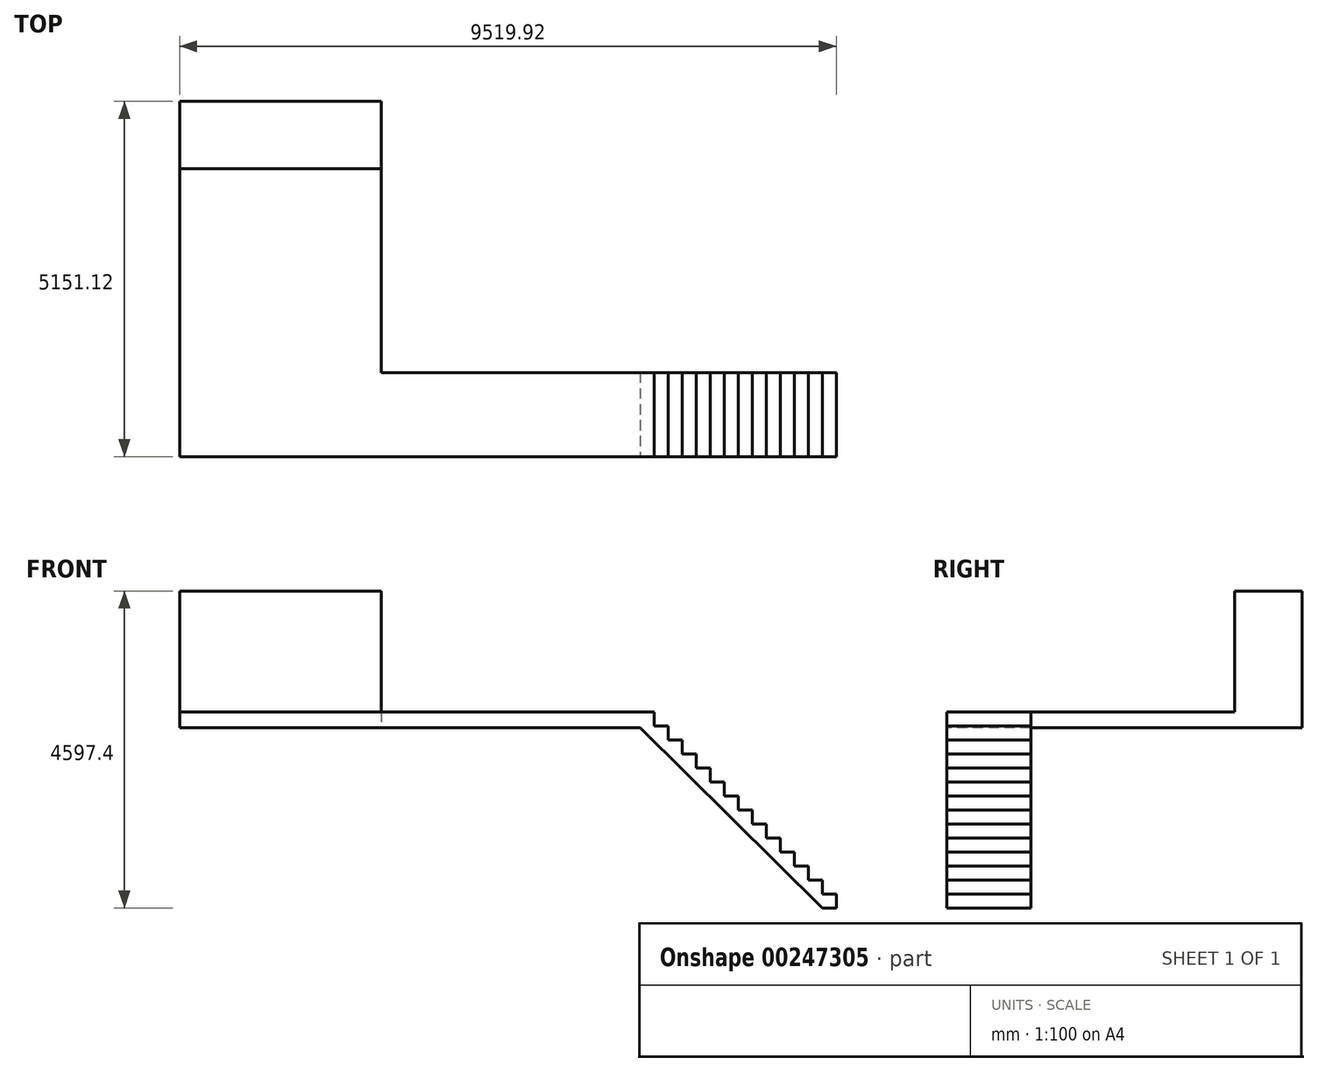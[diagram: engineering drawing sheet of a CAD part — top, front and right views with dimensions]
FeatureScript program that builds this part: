
annotation { "Feature Type Name" : "Feature", "Feature Type Description" : "" }
export const myFeature = defineFeature(function(context is Context, id is Id, definition is map)
    precondition{}
    {
        {
            var Q0;
            Q0=qCreatedBy(makeId("Top.planeOp"),FACE);
            var sketch = newSketch(context, id + "F0", { "sketchPlane" : qUnion([Q0])});
            skLineSegment(sketch, "E0.bottom", {"start": v(1463.04, -2575.56) * mm, "end": v(-1463.04, -2575.56) * mm});
            skLineSegment(sketch, "E0.top", {"start": v(1463.04, 2575.56) * mm, "end": v(-1463.04, 2575.56) * mm});
            skLineSegment(sketch, "E0.left", {"start": v(1463.04, -1356.36) * mm, "end": v(1463.04, 2575.56) * mm});
            skLineSegment(sketch, "E0.right", {"start": v(-1463.04, -2575.56) * mm, "end": v(-1463.04, 2575.56) * mm});
            skPoint(sketch, "E0.middle", {"position": v(0, 0) * mm});
            skLineSegment(sketch, "E1", {"start": v(1463.04, -1356.36) * mm, "end": v(5212.08, -1356.36) * mm});
            skLineSegment(sketch, "E2", {"start": v(1463.04, -2575.56) * mm, "end": v(5212.08, -2575.56) * mm});
            skLineSegment(sketch, "E3", {"start": v(5212.08, -1356.36) * mm, "end": v(5212.08, -2575.56) * mm});
            skSolve(sketch);
        }
        {
            var Q0;
            Q0 = qSketchRegion(id + "F0", true);
            extrude(context, id + "F1", {"entities" : qUnion([Q0]), "depth" : 228.6 * mm});
        }
        {
            var Q0;
            Q0=makeQuery(id+"F1.opExtrude","SWEPT_FACE",FACE,{"disambiguationData":[OSD([sQuery(id+"F0.wireOp",EDGE,"E0.bottom"),sQuery(id+"F0.wireOp",EDGE,"E2")])]});
            var sketch = newSketch(context, id + "F2", { "sketchPlane" : qUnion([Q0])});
            skLineSegment(sketch, "E4", {"start": v(5212.08, 228.6) * mm, "end": v(5415.28, 228.6) * mm});
            skLineSegment(sketch, "E5", {"start": v(5415.28, 228.6) * mm, "end": v(5415.28, 25.4) * mm});
            skLineSegment(sketch, "E6", {"start": v(5415.28, 25.4) * mm, "end": v(5618.48, 25.4) * mm});
            skLineSegment(sketch, "E7", {"start": v(5618.48, 25.4) * mm, "end": v(5618.48, -177.8) * mm});
            skLineSegment(sketch, "E8", {"start": v(5618.48, -177.8) * mm, "end": v(5821.68, -177.8) * mm});
            skLineSegment(sketch, "E9", {"start": v(5821.68, -177.8) * mm, "end": v(5821.68, -381) * mm});
            skLineSegment(sketch, "E10", {"start": v(5821.68, -381) * mm, "end": v(6024.88, -381) * mm});
            skLineSegment(sketch, "E11", {"start": v(6024.88, -381) * mm, "end": v(6024.88, -584.2) * mm});
            skLineSegment(sketch, "E12", {"start": v(6024.88, -584.2) * mm, "end": v(6228.08, -584.2) * mm});
            skLineSegment(sketch, "E13", {"start": v(6228.08, -584.2) * mm, "end": v(6228.08, -787.4) * mm});
            skLineSegment(sketch, "E14", {"start": v(6228.08, -787.4) * mm, "end": v(6431.28, -787.4) * mm});
            skLineSegment(sketch, "E15", {"start": v(6431.28, -787.4) * mm, "end": v(6431.28, -990.6) * mm});
            skLineSegment(sketch, "E16", {"start": v(6431.28, -990.6) * mm, "end": v(6634.48, -990.6) * mm});
            skLineSegment(sketch, "E17", {"start": v(6634.48, -990.6) * mm, "end": v(6634.48, -1193.8) * mm});
            skLineSegment(sketch, "E18", {"start": v(6634.48, -1193.8) * mm, "end": v(6837.68, -1193.8) * mm});
            skLineSegment(sketch, "E19", {"start": v(6837.68, -1193.8) * mm, "end": v(6837.68, -1397) * mm});
            skLineSegment(sketch, "E20", {"start": v(6837.68, -1397) * mm, "end": v(7040.88, -1397) * mm});
            skLineSegment(sketch, "E21", {"start": v(7040.88, -1397) * mm, "end": v(7040.88, -1600.2) * mm});
            skLineSegment(sketch, "E22", {"start": v(7040.88, -1600.2) * mm, "end": v(7244.08, -1600.2) * mm});
            skLineSegment(sketch, "E23", {"start": v(7244.08, -1600.2) * mm, "end": v(7244.08, -1803.4) * mm});
            skLineSegment(sketch, "E24", {"start": v(7244.08, -1803.4) * mm, "end": v(7447.28, -1803.4) * mm});
            skLineSegment(sketch, "E25", {"start": v(7447.28, -1803.4) * mm, "end": v(7447.28, -2006.6) * mm});
            skLineSegment(sketch, "E26", {"start": v(7447.28, -2006.6) * mm, "end": v(7650.48, -2006.6) * mm});
            skLineSegment(sketch, "E27", {"start": v(7650.48, -2006.6) * mm, "end": v(7650.48, -2209.8) * mm});
            skLineSegment(sketch, "E28", {"start": v(7650.48, -2209.8) * mm, "end": v(7853.68, -2209.8) * mm});
            skLineSegment(sketch, "E29", {"start": v(7853.68, -2209.8) * mm, "end": v(7853.68, -2413) * mm});
            skLineSegment(sketch, "E30", {"start": v(7853.68, -2413) * mm, "end": v(8056.88, -2413) * mm});
            skLineSegment(sketch, "E31", {"start": v(8056.88, -2413) * mm, "end": v(8056.88, -2616.2) * mm});
            skLineSegment(sketch, "E32", {"start": v(5212.08, 0) * mm, "end": v(7853.68, -2616.2) * mm});
            skLineSegment(sketch, "E33", {"start": v(7853.68, -2616.2) * mm, "end": v(8056.88, -2616.2) * mm});
            skSolve(sketch);
        }
        {
            var Q0;
            Q0=makeQuery(id+"F2.imprint","IMPRINT",FACE,{"disambiguationData":[TD([[makeQuery(id+"F2.imprint","IMPRINT",EDGE,{"derivedFrom":sQuery(id+"F2.wireOp",EDGE,"E4")}),-1.0]])]});
            var Q1;
            Q1=makeQuery(id+"F1.opExtrude","SWEPT_FACE",FACE,{"disambiguationData":[OSD([sQuery(id+"F0.wireOp",EDGE,"E1")])]});
            extrude(context, id + "F3", {"entities" : qUnion([Q0]), "operationType" : NewBodyOperationType.ADD, "endBound" : BoundingType.UP_TO_SURFACE, "oppositeDirection" : true, "endBoundEntityFace" : qUnion([Q1]), "depth" : 25.4 * mm});
        }
        {
            var Q0;
            Q0=makeQuery(id+"F1.opExtrude","SWEPT_FACE",FACE,{"disambiguationData":[OSD([sQuery(id+"F0.wireOp",EDGE,"E0.left")])]});
            var sketch = newSketch(context, id + "F4", { "sketchPlane" : qUnion([Q0])});
            skLineSegment(sketch, "E34.bottom", {"start": v(2575.56, 228.6) * mm, "end": v(1600.2, 228.6) * mm});
            skLineSegment(sketch, "E34.top", {"start": v(2575.56, 1981.2) * mm, "end": v(1600.2, 1981.2) * mm});
            skLineSegment(sketch, "E34.left", {"start": v(2575.56, 228.6) * mm, "end": v(2575.56, 1981.2) * mm});
            skLineSegment(sketch, "E34.right", {"start": v(1600.2, 228.6) * mm, "end": v(1600.2, 1981.2) * mm});
            skSolve(sketch);
        }
        {
            var Q0;
            Q0=makeQuery(id+"F4.imprint","IMPRINT",FACE,{"disambiguationData":[TD([[makeQuery(id+"F4.imprint","IMPRINT",EDGE,{"derivedFrom":sQuery(id+"F4.wireOp",EDGE,"E34.bottom")}),1.0]])]});
            var Q1;
            Q1=makeQuery(id+"F1.opExtrude","SWEPT_FACE",FACE,{"disambiguationData":[OSD([sQuery(id+"F0.wireOp",EDGE,"E0.right")])]});
            extrude(context, id + "F5", {"entities" : qUnion([Q0]), "operationType" : NewBodyOperationType.ADD, "endBound" : BoundingType.UP_TO_SURFACE, "oppositeDirection" : true, "endBoundEntityFace" : qUnion([Q1]), "depth" : 25.4 * mm});
        }
    });
